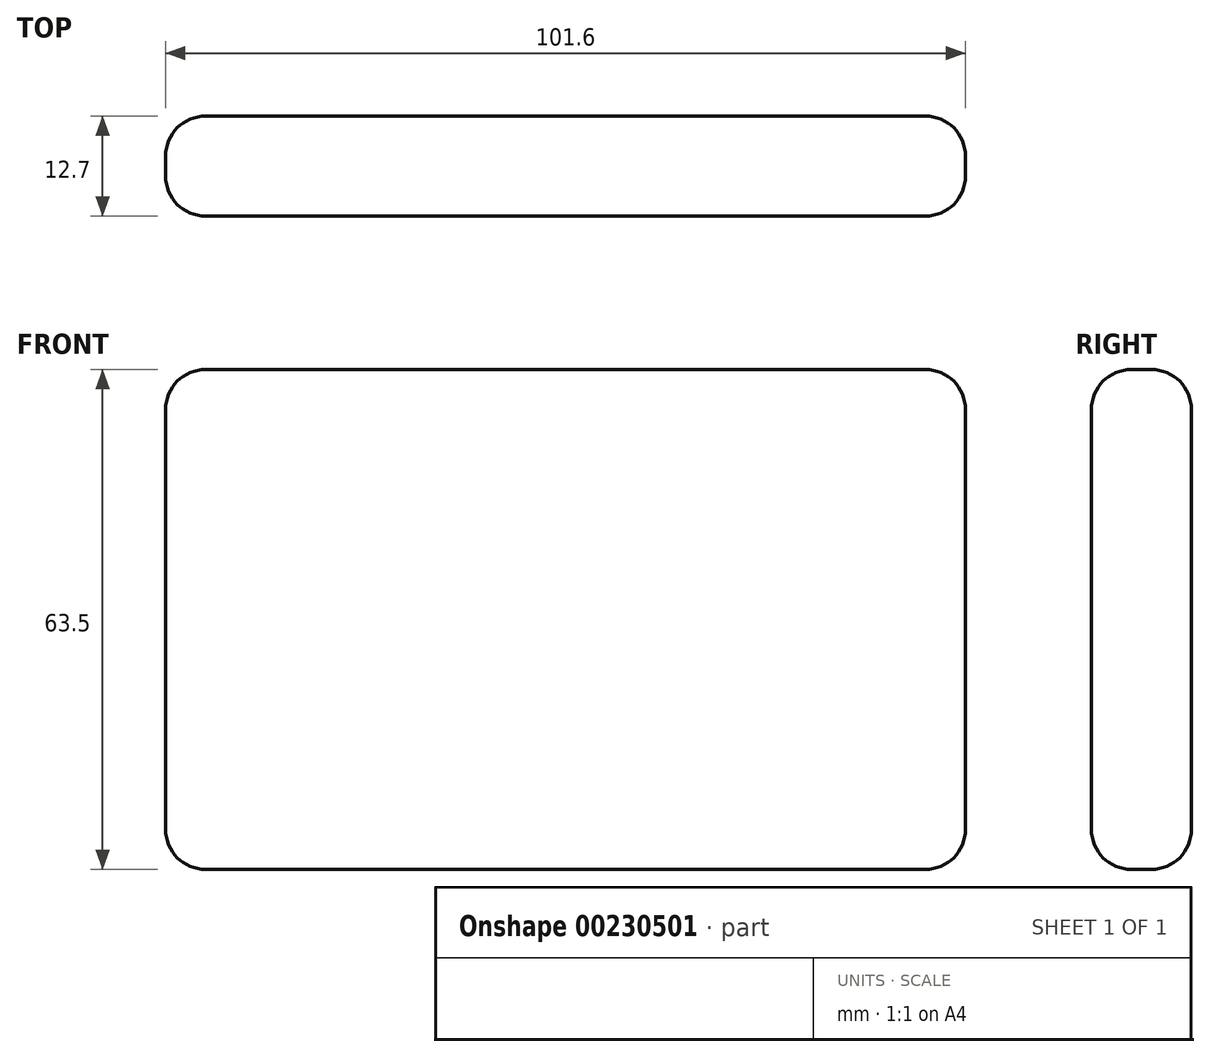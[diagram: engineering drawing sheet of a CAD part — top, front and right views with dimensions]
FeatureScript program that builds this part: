
annotation { "Feature Type Name" : "Feature", "Feature Type Description" : "" }
export const myFeature = defineFeature(function(context is Context, id is Id, definition is map)
    precondition{}
    {
        {
            var Q0;
            Q0=qCreatedBy(makeId("Front.planeOp"),FACE);
            var sketch = newSketch(context, id + "F0", { "sketchPlane" : qUnion([Q0])});
            skLineSegment(sketch, "E0.bottom", {"start": v(-50.8, 31.75) * mm, "end": v(50.8, 31.75) * mm});
            skLineSegment(sketch, "E0.top", {"start": v(-50.8, -31.75) * mm, "end": v(50.8, -31.75) * mm});
            skLineSegment(sketch, "E0.left", {"start": v(-50.8, 31.75) * mm, "end": v(-50.8, -31.75) * mm});
            skLineSegment(sketch, "E0.right", {"start": v(50.8, 31.75) * mm, "end": v(50.8, -31.75) * mm});
            skPoint(sketch, "E0.middle", {"position": v(0, 0) * mm});
            skSolve(sketch);
        }
        {
            var Q0;
            Q0=makeQuery(id+"F0.imprint","IMPRINT",FACE,{"disambiguationData":[TD([[makeQuery(id+"F0.imprint","IMPRINT",EDGE,{"derivedFrom":sQuery(id+"F0.wireOp",EDGE,"E0.bottom")}),-1.0]])]});
            extrude(context, id + "F1", {"entities" : qUnion([Q0]), "endBound" : BoundingType.SYMMETRIC, "depth" : 12.7 * mm});
        }
        {
            var Q0;
            Q0=makeQuery(id+"F1.opExtrude","CAP_EDGE",EDGE,{"disambiguationData":[OSD([sQuery(id+"F0.wireOp",EDGE,"E0.bottom")])],"isStart":false});
            var Q1;
            Q1=makeQuery(id+"F1.opExtrude","CAP_EDGE",EDGE,{"disambiguationData":[OSD([sQuery(id+"F0.wireOp",EDGE,"E0.top")])],"isStart":false});
            var Q2;
            Q2=makeQuery(id+"F1.opExtrude","CAP_EDGE",EDGE,{"disambiguationData":[OSD([sQuery(id+"F0.wireOp",EDGE,"E0.left")])],"isStart":false});
            var Q3;
            Q3=makeQuery(id+"F1.opExtrude","CAP_EDGE",EDGE,{"disambiguationData":[OSD([sQuery(id+"F0.wireOp",EDGE,"E0.right")])],"isStart":false});
            var Q4;
            Q4=makeQuery(id+"F1.opExtrude","CAP_EDGE",EDGE,{"disambiguationData":[OSD([sQuery(id+"F0.wireOp",EDGE,"E0.right")])],"isStart":true});
            var Q5;
            Q5=makeQuery(id+"F1.opExtrude","CAP_EDGE",EDGE,{"disambiguationData":[OSD([sQuery(id+"F0.wireOp",EDGE,"E0.bottom")])],"isStart":true});
            var Q6;
            Q6=makeQuery(id+"F1.opExtrude","SWEPT_EDGE",EDGE,{"disambiguationData":[OSD([sQuery(id+"F0.wireOp",EDGE,"E0.top"),sQuery(id+"F0.wireOp",EDGE,"E0.right")])]});
            var Q7;
            Q7=makeQuery(id+"F1.opExtrude","SWEPT_EDGE",EDGE,{"disambiguationData":[OSD([sQuery(id+"F0.wireOp",EDGE,"E0.bottom"),sQuery(id+"F0.wireOp",EDGE,"E0.right")])]});
            var Q8;
            Q8=makeQuery(id+"F1.opExtrude","CAP_EDGE",EDGE,{"disambiguationData":[OSD([sQuery(id+"F0.wireOp",EDGE,"E0.top")])],"isStart":true});
            var Q9;
            Q9=makeQuery(id+"F1.opExtrude","SWEPT_EDGE",EDGE,{"disambiguationData":[OSD([sQuery(id+"F0.wireOp",EDGE,"E0.top"),sQuery(id+"F0.wireOp",EDGE,"E0.left")])]});
            var Q10;
            Q10=makeQuery(id+"F1.opExtrude","CAP_EDGE",EDGE,{"disambiguationData":[OSD([sQuery(id+"F0.wireOp",EDGE,"E0.left")])],"isStart":true});
            var Q11;
            Q11=makeQuery(id+"F1.opExtrude","SWEPT_EDGE",EDGE,{"disambiguationData":[OSD([sQuery(id+"F0.wireOp",EDGE,"E0.bottom"),sQuery(id+"F0.wireOp",EDGE,"E0.left")])]});
            fillet(context, id + "F2", {"entities" : qUnion([Q0, Q1, Q2, Q3, Q4, Q5, Q6, Q7, Q8, Q9, Q10, Q11]), "radius" : 5.08 * mm, "tangentPropagation" : true, "allowEdgeOverflow" : false});
        }
    });
